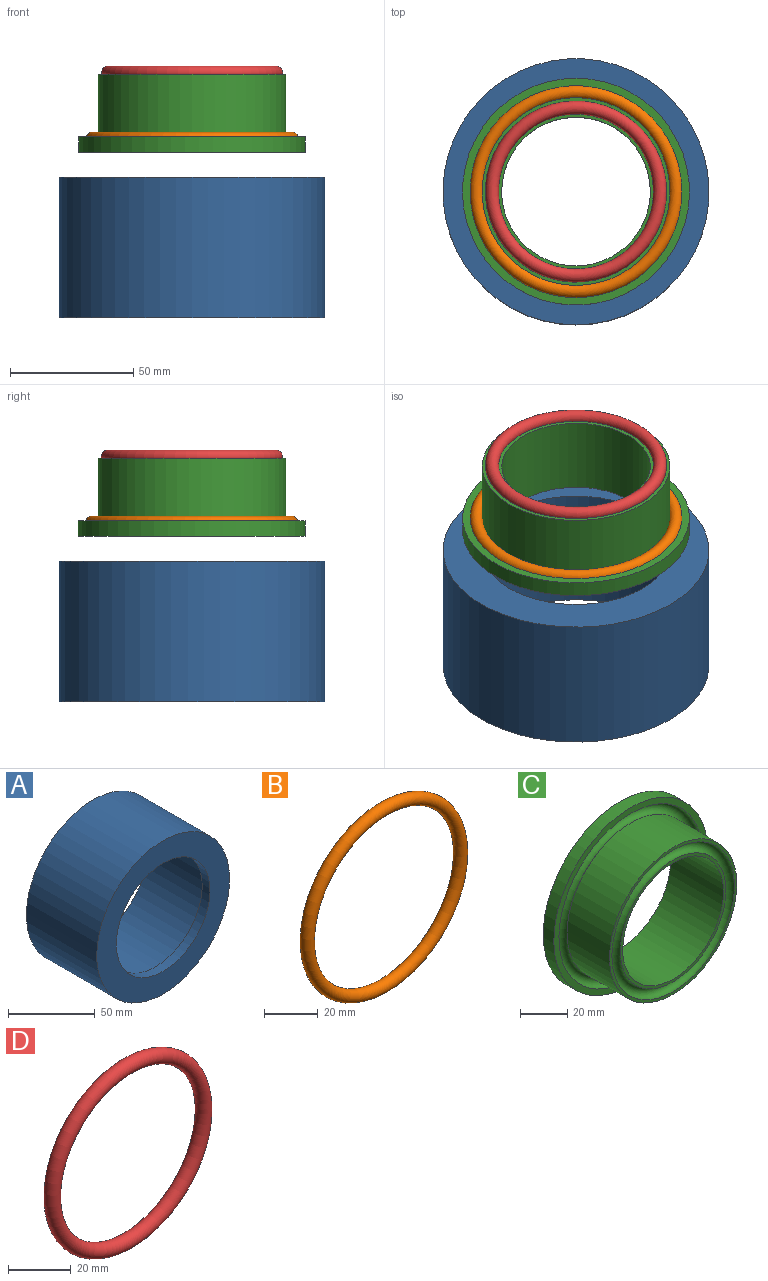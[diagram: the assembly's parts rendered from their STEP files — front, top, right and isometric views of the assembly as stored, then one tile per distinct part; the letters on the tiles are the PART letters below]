
ASSEMBLY  parts=4 mates=3
PART A: 6 faces, bbox 108x57.2x108 mm
  f0: plane 92.1x92.1mm, normal (0,1,0), area 2101.8mm2, adj f1,f4
  f1: cylinder r=38.1mm len=76.2mm, axis (0,1,0), area 1520.1mm2, adj f0,f3
  f2: cylinder r=54mm len=108mm, axis (0,1,0), area 19390.7mm2, adj f3,f5
  f3: plane 108x108mm, normal (0,-1,0), area 4600.7mm2, adj f1,f2
  f4: cylinder r=46.05mm len=92.1mm, axis (0,-1,0), area 14698.6mm2, adj f0,f5
  f5: plane 108x108mm, normal (0,1,0), area 2498.9mm2, adj f2,f4
PART B: 1 faces, bbox 93.3x5.3x93.3 mm
  f0: torus R=40.45mm, axis (0,-1,0), area 4258.9mm2
PART C: 10 faces, bbox 93.3x32.9x93.3 mm
  f0: plane 76.2x76.2mm, normal (0,-1,0), area 332mm2, adj f3,f4
  f1: plane 63.15x63.15mm, normal (0,-1,0), area 274mm2, adj f2,f4
  f2: cylinder r=30.16mm len=60.33mm, axis (0,-1,0), area 6017.2mm2, adj f1,f6
  f3: cylinder r=38.1mm len=76.2mm, axis (0,-1,0), area 6080.5mm2, adj f0,f8
  f4: torus R=34.13mm, axis (0,-1,0), area 2128.3mm2, adj f0,f1
  f5: cylinder r=46.05mm len=92.1mm, axis (0,-1,0), area 1837.3mm2, adj f6,f7
  f6: plane 92.1x92.1mm, normal (0,1,0), area 3804mm2, adj f2,f5
  f7: plane 92.1x92.1mm, normal (0,-1,0), area 851.9mm2, adj f5,f9
  f8: plane 76.2x76.2mm, normal (0,1,0), area 49.3mm2, adj f3,f9
  f9: torus R=40.45mm, axis (0,-1,0), area 2522.2mm2, adj f7,f8
PART D: 1 faces, bbox 79.6x5.3x79.6 mm
  f0: torus R=34.1mm, axis (0,-1,0), area 3590.3mm2
PLACE A rot(axis=(-1,0,0),90deg) t=(-0.76,-0.34,-26.85)mm
PLACE B rot(axis=(-1,0,0),90deg) t=(-0.76,-0.34,-4.91)mm
PLACE C rot(axis=(-1,0,0),90deg) t=(-0.76,-0.34,21.26)mm fixed
PLACE D rot(axis=(1,0,0),90deg) t=(-0.76,-0.34,21.9)mm
MATE slider A.f2 <-> C.f3  axis (0,0,-1) through (-0.76,-0.34,-49.08)mm
MATE slider B.f0 <-> C.f3  axis (0,0,1) through (-0.76,-0.34,-4.91)mm
MATE slider D.f0 <-> C.f4  axis (0,0,-1) through (-0.76,-0.34,21.9)mm
